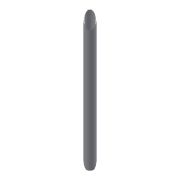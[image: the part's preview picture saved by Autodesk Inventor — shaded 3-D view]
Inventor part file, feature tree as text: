
AUTODESK INVENTOR PART (.ipt)
format: ipt  version: 2015 (Build 190159000, 159)  size: 115,712 bytes
history: native  units: mm
features: sketch x2, other x1, extrude x1, shell x1, hole x1
ambient origin geometry x8: Origin, YZ Plane, XZ Plane, XY Plane, X Axis, Y Axis, Z Axis, Center Point
bodies: Body1 (feature_tree)
feature tree (6):
  other  "Bryła2"
  extrude  "Wyciągnięcie proste2"  Depth=32.0mm
  shell  "Skorupa2"  Thickness=460.0mm
  hole  "Otwór1"  [1 undecoded]
  sketch  "Szkic2"
  sketch  "Szkic3"
note: 1 required parameter value undecoded (feature->parameter linkage not recoverable at this tier; creation-order binding heuristic only, values carry confidence <= 0.55)
